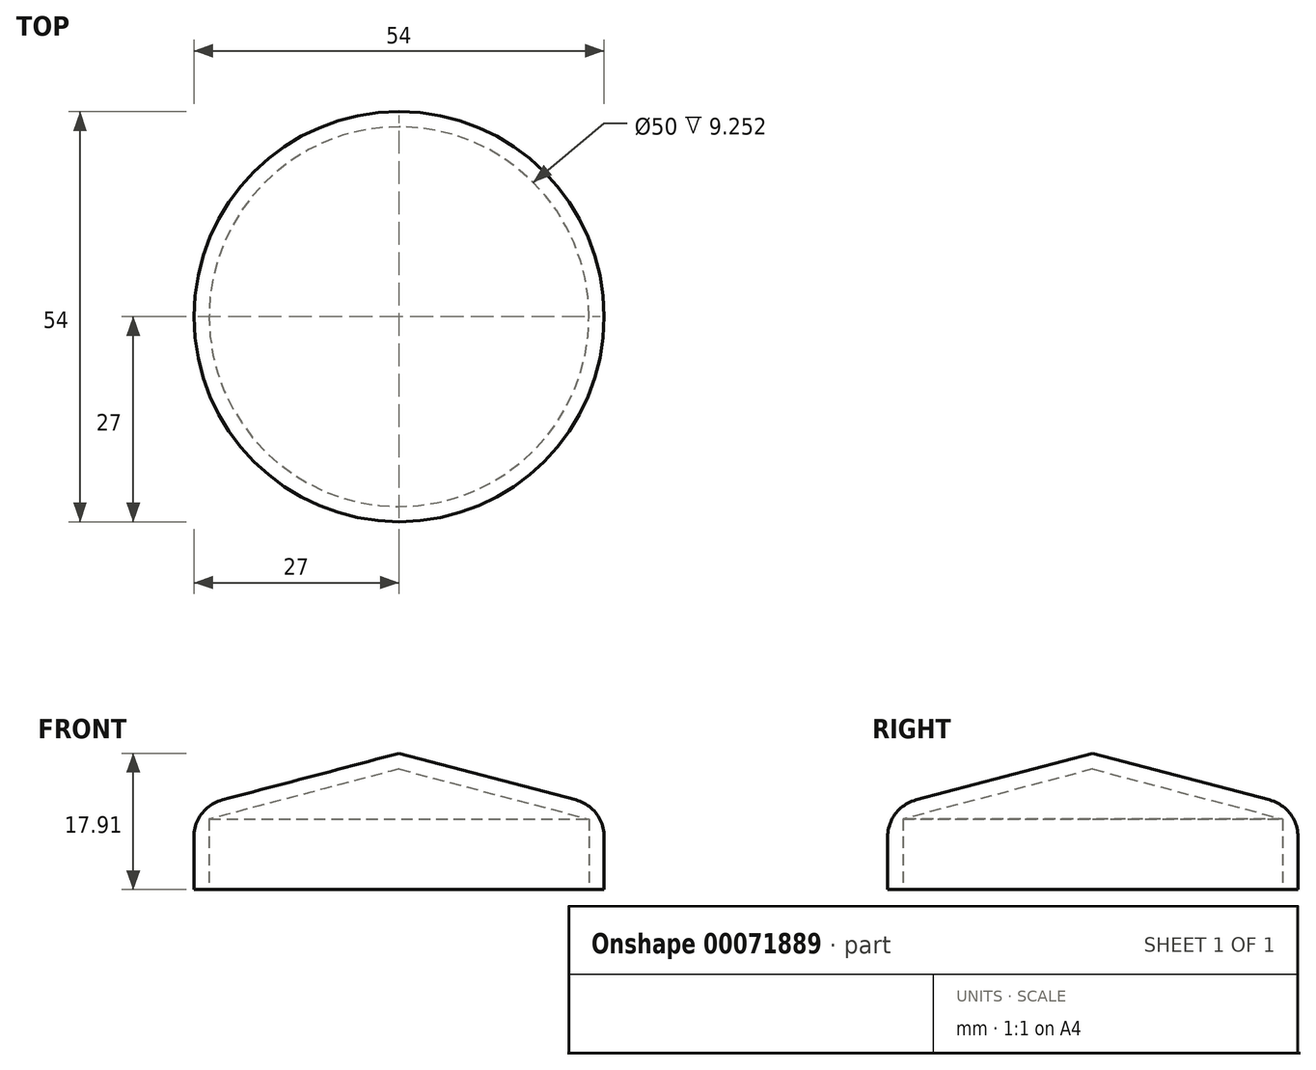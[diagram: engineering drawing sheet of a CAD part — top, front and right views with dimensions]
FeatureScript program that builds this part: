
annotation { "Feature Type Name" : "Feature", "Feature Type Description" : "" }
export const myFeature = defineFeature(function(context is Context, id is Id, definition is map)
    precondition{}
    {
        {
            var Q0;
            Q0=qCreatedBy(makeId("Front.planeOp"),FACE);
            var sketch = newSketch(context, id + "F0", { "sketchPlane" : qUnion([Q0])});
            skLineSegment(sketch, "E0", {"start": v(27, 0) * mm, "end": v(27, 10.8) * mm});
            skLineSegment(sketch, "E1", {"start": v(27, 10.8) * mm, "end": v(0, 17.91) * mm});
            skLineSegment(sketch, "E2", {"start": v(27, 0) * mm, "end": v(25, 0) * mm});
            skLineSegment(sketch, "E3", {"start": v(0, 17.91) * mm, "end": v(0, 15.84) * mm});
            skLineSegment(sketch, "E4", {"start": v(0, 15.84) * mm, "end": v(25, 9.25) * mm});
            skLineSegment(sketch, "E5", {"start": v(25, 0) * mm, "end": v(25, 9.25) * mm});
            skSolve(sketch);
        }
        {
            var Q0;
            Q0=qCreatedBy(makeId("Front.planeOp"),FACE);
            var sketch = newSketch(context, id + "F1", { "sketchPlane" : qUnion([Q0])});
            skLineSegment(sketch, "E6", {"start": v(0, 0) * mm, "end": v(0, 56.8) * mm, "construction": true});
            skSolve(sketch);
        }
        {
            var Q0;
            Q0 = qSketchRegion(id + "F0", true);
            var Q1;
            Q1 = qConstructionFilter(qBodyType(qCreatedBy(id + "F0" ,EDGE), BodyType.WIRE), ConstructionObject.NO);
            var Q2;
            Q2=sQuery(id+"F1.wireOp",EDGE,"E6");
            revolve(context, id + "F2", {"entities" : qUnion([Q0]), "surfaceEntities" : qUnion([Q1]), "axis" : qUnion([Q2]), "revolveType" : RevolveType.FULL});
        }
        {
            var Q0;
            Q0=makeQuery(id+"F2.opRevolve","SWEPT_EDGE",EDGE,{"disambiguationData":[OSD([sQuery(id+"F0.wireOp",EDGE,"E0"),sQuery(id+"F0.wireOp",EDGE,"E1")])]});
            fillet(context, id + "F3", {"entities" : qUnion([Q0]), "radius" : 5 * mm, "tangentPropagation" : true, "allowEdgeOverflow" : false});
        }
    });
